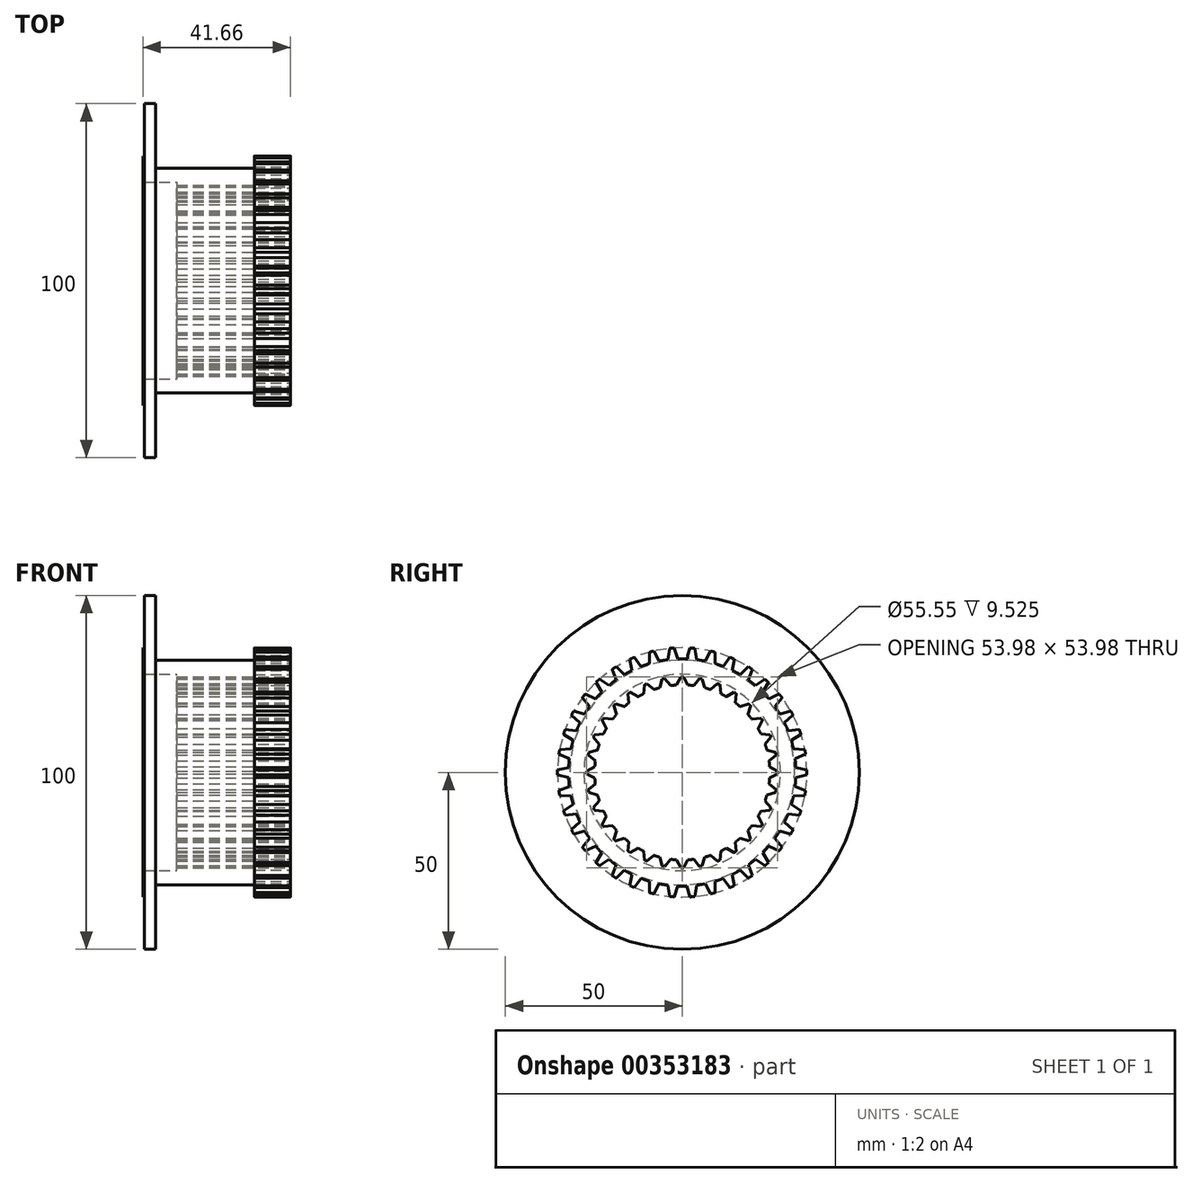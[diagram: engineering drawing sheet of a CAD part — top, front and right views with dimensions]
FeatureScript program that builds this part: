
annotation { "Feature Type Name" : "Feature", "Feature Type Description" : "" }
export const myFeature = defineFeature(function(context is Context, id is Id, definition is map)
    precondition{}
    {
        {
            var Q0;
            Q0=qCreatedBy(makeId("Front.planeOp"),FACE);
            var sketch = newSketch(context, id + "F0", { "sketchPlane" : qUnion([Q0])});
            skLineSegment(sketch, "E0", {"start": v(0, 0) * mm, "end": v(0, 35.24) * mm});
            skLineSegment(sketch, "E1", {"start": v(0, 35.24) * mm, "end": v(0.38, 35.24) * mm});
            skLineSegment(sketch, "E2", {"start": v(0.38, 35.24) * mm, "end": v(0.38, 50) * mm});
            skLineSegment(sketch, "E3", {"start": v(0.38, 50) * mm, "end": v(3.56, 50) * mm});
            skLineSegment(sketch, "E4", {"start": v(3.56, 50) * mm, "end": v(3.56, 31.75) * mm});
            skLineSegment(sketch, "E5", {"start": v(3.56, 31.75) * mm, "end": v(31.5, 31.75) * mm});
            skLineSegment(sketch, "E6", {"start": v(31.5, 31.75) * mm, "end": v(31.5, 35.24) * mm});
            skLineSegment(sketch, "E7", {"start": v(31.5, 35.24) * mm, "end": v(41.66, 35.24) * mm});
            skLineSegment(sketch, "E8", {"start": v(41.66, 35.24) * mm, "end": v(41.66, 0) * mm});
            skLineSegment(sketch, "E9", {"start": v(41.66, 0) * mm, "end": v(0, 0) * mm});
            skLineSegment(sketch, "E10", {"start": v(0, 27.77) * mm, "end": v(9.52, 27.77) * mm});
            skLineSegment(sketch, "E11", {"start": v(9.52, 27.77) * mm, "end": v(9.52, 24.77) * mm});
            skLineSegment(sketch, "E12", {"start": v(9.52, 24.77) * mm, "end": v(41.66, 24.77) * mm});
            skSolve(sketch);
        }
        {
            var Q0;
            {var subQ4=sQuery(id+"F0.wireOp",EDGE,"E1");Q0=makeQuery(id+"F0.imprint","IMPRINT",FACE,{"disambiguationData":[TD([[makeQuery(id+"F0.imprint","IMPRINT",EDGE,{"derivedFrom":subQ4}),-1.0]])]});}
            var Q1;
            Q1=sQuery(id+"F0.wireOp",EDGE,"E9");
            revolve(context, id + "F1", {"entities" : qUnion([Q0]), "axis" : qUnion([Q1]), "revolveType" : RevolveType.FULL});
        }
        {
            var Q0;
            Q0=makeQuery(id+"F1.opRevolve","SWEPT_FACE",FACE,{"disambiguationData":[OSD([sQuery(id+"F0.wireOp",EDGE,"E8")])]});
            var sketch = newSketch(context, id + "F2", { "sketchPlane" : qUnion([Q0])});
            skCircle(sketch, "E13", {"center": v(0, 0) * mm, "radius": 32.13 * mm});
            skLineSegment(sketch, "E14", {"start": v(-2.22, 35.17) * mm, "end": v(-1.27, 32.1) * mm});
            skLineSegment(sketch, "E15.MirrorCS", {"start": v(2.22, 35.17) * mm, "end": v(1.27, 32.1) * mm});
            skLineSegment(sketch, "E16.1.0", {"start": v(-7.98, 34.33) * mm, "end": v(-6.54, 31.46) * mm});
            skLineSegment(sketch, "E16.1.1", {"start": v(-3.6, 35.06) * mm, "end": v(-4.03, 31.88) * mm});
            skLineSegment(sketch, "E16.2.0", {"start": v(-13.52, 32.54) * mm, "end": v(-11.63, 29.95) * mm});
            skLineSegment(sketch, "E16.2.1", {"start": v(-9.32, 33.99) * mm, "end": v(-9.22, 30.78) * mm});
            skLineSegment(sketch, "E16.3.0", {"start": v(-18.7, 29.88) * mm, "end": v(-16.4, 27.63) * mm});
            skLineSegment(sketch, "E16.3.1", {"start": v(-14.79, 32) * mm, "end": v(-14.16, 28.84) * mm});
            skLineSegment(sketch, "E16.4.0", {"start": v(-23.36, 26.4) * mm, "end": v(-20.72, 24.56) * mm});
            skLineSegment(sketch, "E16.4.1", {"start": v(-19.85, 29.12) * mm, "end": v(-18.72, 26.12) * mm});
            skLineSegment(sketch, "E16.5.0", {"start": v(-27.38, 22.19) * mm, "end": v(-24.48, 20.81) * mm});
            skLineSegment(sketch, "E16.5.1", {"start": v(-24.37, 25.46) * mm, "end": v(-22.76, 22.68) * mm});
            skLineSegment(sketch, "E16.6.0", {"start": v(-30.66, 17.38) * mm, "end": v(-27.57, 16.5) * mm});
            skLineSegment(sketch, "E16.6.1", {"start": v(-28.23, 21.1) * mm, "end": v(-26.18, 18.62) * mm});
            skLineSegment(sketch, "E16.7.0", {"start": v(-33.1, 12.1) * mm, "end": v(-29.91, 11.73) * mm});
            skLineSegment(sketch, "E16.7.1", {"start": v(-31.32, 16.16) * mm, "end": v(-28.9, 14.06) * mm});
            skLineSegment(sketch, "E16.8.0", {"start": v(-34.64, 6.48) * mm, "end": v(-31.44, 6.65) * mm});
            skLineSegment(sketch, "E16.8.1", {"start": v(-33.55, 10.79) * mm, "end": v(-30.81, 9.11) * mm});
            skLineSegment(sketch, "E16.9.0", {"start": v(-35.24, 0.69) * mm, "end": v(-32.1, 1.39) * mm});
            skLineSegment(sketch, "E16.9.1", {"start": v(-34.87, 5.12) * mm, "end": v(-31.9, 3.92) * mm});
            skLineSegment(sketch, "E16.10.0", {"start": v(-34.87, -5.12) * mm, "end": v(-31.9, -3.92) * mm});
            skLineSegment(sketch, "E16.10.1", {"start": v(-35.24, -0.69) * mm, "end": v(-32.1, -1.39) * mm});
            skLineSegment(sketch, "E16.11.0", {"start": v(-33.55, -10.79) * mm, "end": v(-30.81, -9.11) * mm});
            skLineSegment(sketch, "E16.11.1", {"start": v(-34.64, -6.48) * mm, "end": v(-31.44, -6.65) * mm});
            skLineSegment(sketch, "E16.12.0", {"start": v(-31.32, -16.16) * mm, "end": v(-28.9, -14.06) * mm});
            skLineSegment(sketch, "E16.12.1", {"start": v(-33.1, -12.1) * mm, "end": v(-29.91, -11.73) * mm});
            skLineSegment(sketch, "E16.13.0", {"start": v(-28.23, -21.1) * mm, "end": v(-26.18, -18.62) * mm});
            skLineSegment(sketch, "E16.13.1", {"start": v(-30.66, -17.38) * mm, "end": v(-27.57, -16.5) * mm});
            skLineSegment(sketch, "E16.14.0", {"start": v(-24.37, -25.46) * mm, "end": v(-22.76, -22.68) * mm});
            skLineSegment(sketch, "E16.14.1", {"start": v(-27.38, -22.19) * mm, "end": v(-24.48, -20.81) * mm});
            skLineSegment(sketch, "E16.15.0", {"start": v(-19.85, -29.12) * mm, "end": v(-18.72, -26.12) * mm});
            skLineSegment(sketch, "E16.15.1", {"start": v(-23.36, -26.4) * mm, "end": v(-20.72, -24.56) * mm});
            skLineSegment(sketch, "E16.16.0", {"start": v(-14.79, -32) * mm, "end": v(-14.16, -28.84) * mm});
            skLineSegment(sketch, "E16.16.1", {"start": v(-18.7, -29.88) * mm, "end": v(-16.4, -27.63) * mm});
            skLineSegment(sketch, "E16.17.0", {"start": v(-9.32, -33.99) * mm, "end": v(-9.22, -30.78) * mm});
            skLineSegment(sketch, "E16.17.1", {"start": v(-13.52, -32.54) * mm, "end": v(-11.63, -29.95) * mm});
            skLineSegment(sketch, "E16.18.0", {"start": v(-3.6, -35.06) * mm, "end": v(-4.03, -31.88) * mm});
            skLineSegment(sketch, "E16.18.1", {"start": v(-7.98, -34.33) * mm, "end": v(-6.54, -31.46) * mm});
            skLineSegment(sketch, "E16.19.0", {"start": v(2.22, -35.17) * mm, "end": v(1.27, -32.1) * mm});
            skLineSegment(sketch, "E16.19.1", {"start": v(-2.22, -35.17) * mm, "end": v(-1.27, -32.1) * mm});
            skLineSegment(sketch, "E16.20.0", {"start": v(7.98, -34.33) * mm, "end": v(6.54, -31.46) * mm});
            skLineSegment(sketch, "E16.20.1", {"start": v(3.6, -35.06) * mm, "end": v(4.03, -31.88) * mm});
            skLineSegment(sketch, "E16.21.0", {"start": v(13.52, -32.54) * mm, "end": v(11.63, -29.95) * mm});
            skLineSegment(sketch, "E16.21.1", {"start": v(9.32, -33.99) * mm, "end": v(9.22, -30.78) * mm});
            skLineSegment(sketch, "E16.22.0", {"start": v(18.7, -29.88) * mm, "end": v(16.4, -27.63) * mm});
            skLineSegment(sketch, "E16.22.1", {"start": v(14.79, -32) * mm, "end": v(14.16, -28.84) * mm});
            skLineSegment(sketch, "E16.23.0", {"start": v(23.36, -26.4) * mm, "end": v(20.72, -24.56) * mm});
            skLineSegment(sketch, "E16.23.1", {"start": v(19.85, -29.12) * mm, "end": v(18.72, -26.12) * mm});
            skLineSegment(sketch, "E16.24.0", {"start": v(27.38, -22.19) * mm, "end": v(24.48, -20.81) * mm});
            skLineSegment(sketch, "E16.24.1", {"start": v(24.37, -25.46) * mm, "end": v(22.76, -22.68) * mm});
            skLineSegment(sketch, "E16.25.0", {"start": v(30.66, -17.38) * mm, "end": v(27.57, -16.5) * mm});
            skLineSegment(sketch, "E16.25.1", {"start": v(28.23, -21.1) * mm, "end": v(26.18, -18.62) * mm});
            skLineSegment(sketch, "E16.26.0", {"start": v(33.1, -12.1) * mm, "end": v(29.91, -11.73) * mm});
            skLineSegment(sketch, "E16.26.1", {"start": v(31.32, -16.16) * mm, "end": v(28.9, -14.06) * mm});
            skLineSegment(sketch, "E16.27.0", {"start": v(34.64, -6.48) * mm, "end": v(31.44, -6.65) * mm});
            skLineSegment(sketch, "E16.27.1", {"start": v(33.55, -10.79) * mm, "end": v(30.81, -9.11) * mm});
            skLineSegment(sketch, "E16.28.0", {"start": v(35.24, -0.69) * mm, "end": v(32.1, -1.39) * mm});
            skLineSegment(sketch, "E16.28.1", {"start": v(34.87, -5.12) * mm, "end": v(31.9, -3.92) * mm});
            skLineSegment(sketch, "E16.29.0", {"start": v(34.87, 5.12) * mm, "end": v(31.9, 3.92) * mm});
            skLineSegment(sketch, "E16.29.1", {"start": v(35.24, 0.69) * mm, "end": v(32.1, 1.39) * mm});
            skLineSegment(sketch, "E16.30.0", {"start": v(33.55, 10.79) * mm, "end": v(30.81, 9.11) * mm});
            skLineSegment(sketch, "E16.30.1", {"start": v(34.64, 6.48) * mm, "end": v(31.44, 6.65) * mm});
            skLineSegment(sketch, "E16.31.0", {"start": v(31.32, 16.16) * mm, "end": v(28.9, 14.06) * mm});
            skLineSegment(sketch, "E16.31.1", {"start": v(33.1, 12.1) * mm, "end": v(29.91, 11.73) * mm});
            skLineSegment(sketch, "E16.32.0", {"start": v(28.23, 21.1) * mm, "end": v(26.18, 18.62) * mm});
            skLineSegment(sketch, "E16.32.1", {"start": v(30.66, 17.38) * mm, "end": v(27.57, 16.5) * mm});
            skLineSegment(sketch, "E16.33.0", {"start": v(24.37, 25.46) * mm, "end": v(22.76, 22.68) * mm});
            skLineSegment(sketch, "E16.33.1", {"start": v(27.38, 22.19) * mm, "end": v(24.48, 20.81) * mm});
            skLineSegment(sketch, "E16.34.0", {"start": v(19.85, 29.12) * mm, "end": v(18.72, 26.12) * mm});
            skLineSegment(sketch, "E16.34.1", {"start": v(23.36, 26.4) * mm, "end": v(20.72, 24.56) * mm});
            skLineSegment(sketch, "E16.35.0", {"start": v(14.79, 32) * mm, "end": v(14.16, 28.84) * mm});
            skLineSegment(sketch, "E16.35.1", {"start": v(18.7, 29.88) * mm, "end": v(16.4, 27.63) * mm});
            skLineSegment(sketch, "E16.36.0", {"start": v(9.32, 33.99) * mm, "end": v(9.22, 30.78) * mm});
            skLineSegment(sketch, "E16.36.1", {"start": v(13.52, 32.54) * mm, "end": v(11.63, 29.95) * mm});
            skLineSegment(sketch, "E16.37.0", {"start": v(3.6, 35.06) * mm, "end": v(4.03, 31.88) * mm});
            skLineSegment(sketch, "E16.37.1", {"start": v(7.98, 34.33) * mm, "end": v(6.54, 31.46) * mm});
            skLineSegment(sketch, "E17", {"start": v(0, 0) * mm, "end": v(0, 59.65) * mm});
            skCircle(sketch, "E18", {"center": v(0, 0) * mm, "radius": 26.99 * mm});
            skLineSegment(sketch, "E19.0", {"start": v(0.38, 0) * mm, "end": v(0.38, 59.65) * mm});
            skLineSegment(sketch, "E20.0", {"start": v(1.57, 0) * mm, "end": v(1.57, 59.65) * mm});
            skLineSegment(sketch, "E21", {"start": v(0.38, 26.98) * mm, "end": v(1.57, 24.71) * mm});
            skLineSegment(sketch, "E22.MirrorCS", {"start": v(-0.38, 26.98) * mm, "end": v(-1.57, 24.71) * mm});
            skLineSegment(sketch, "E23.1.0", {"start": v(-5.64, 26.4) * mm, "end": v(-6.37, 23.93) * mm});
            skLineSegment(sketch, "E23.1.1", {"start": v(-4.9, 26.54) * mm, "end": v(-3.28, 24.55) * mm});
            skLineSegment(sketch, "E23.2.0", {"start": v(-10.68, 24.78) * mm, "end": v(-10.91, 22.23) * mm});
            skLineSegment(sketch, "E23.2.1", {"start": v(-9.97, 25.08) * mm, "end": v(-8, 23.44) * mm});
            skLineSegment(sketch, "E23.3.0", {"start": v(-15.3, 22.23) * mm, "end": v(-15.04, 19.67) * mm});
            skLineSegment(sketch, "E23.3.1", {"start": v(-14.68, 22.65) * mm, "end": v(-12.42, 21.42) * mm});
            skLineSegment(sketch, "E23.4.0", {"start": v(-19.35, 18.81) * mm, "end": v(-18.59, 16.36) * mm});
            skLineSegment(sketch, "E23.4.1", {"start": v(-18.81, 19.35) * mm, "end": v(-16.36, 18.59) * mm});
            skLineSegment(sketch, "E23.5.0", {"start": v(-22.65, 14.68) * mm, "end": v(-21.42, 12.42) * mm});
            skLineSegment(sketch, "E23.5.1", {"start": v(-22.23, 15.3) * mm, "end": v(-19.67, 15.04) * mm});
            skLineSegment(sketch, "E23.6.0", {"start": v(-25.08, 9.97) * mm, "end": v(-23.44, 8) * mm});
            skLineSegment(sketch, "E23.6.1", {"start": v(-24.78, 10.68) * mm, "end": v(-22.23, 10.91) * mm});
            skLineSegment(sketch, "E23.7.0", {"start": v(-26.54, 4.9) * mm, "end": v(-24.55, 3.28) * mm});
            skLineSegment(sketch, "E23.7.1", {"start": v(-26.4, 5.64) * mm, "end": v(-23.93, 6.37) * mm});
            skLineSegment(sketch, "E23.8.0", {"start": v(-26.98, -0.38) * mm, "end": v(-24.71, -1.57) * mm});
            skLineSegment(sketch, "E23.8.1", {"start": v(-26.98, 0.38) * mm, "end": v(-24.71, 1.57) * mm});
            skLineSegment(sketch, "E23.9.0", {"start": v(-26.4, -5.64) * mm, "end": v(-23.93, -6.37) * mm});
            skLineSegment(sketch, "E23.9.1", {"start": v(-26.54, -4.9) * mm, "end": v(-24.55, -3.28) * mm});
            skLineSegment(sketch, "E23.10.0", {"start": v(-24.78, -10.68) * mm, "end": v(-22.23, -10.91) * mm});
            skLineSegment(sketch, "E23.10.1", {"start": v(-25.08, -9.97) * mm, "end": v(-23.44, -8) * mm});
            skLineSegment(sketch, "E23.11.0", {"start": v(-22.23, -15.3) * mm, "end": v(-19.67, -15.04) * mm});
            skLineSegment(sketch, "E23.11.1", {"start": v(-22.65, -14.68) * mm, "end": v(-21.42, -12.42) * mm});
            skLineSegment(sketch, "E23.12.0", {"start": v(-18.81, -19.35) * mm, "end": v(-16.36, -18.59) * mm});
            skLineSegment(sketch, "E23.12.1", {"start": v(-19.35, -18.81) * mm, "end": v(-18.59, -16.36) * mm});
            skLineSegment(sketch, "E23.13.0", {"start": v(-14.68, -22.65) * mm, "end": v(-12.42, -21.42) * mm});
            skLineSegment(sketch, "E23.13.1", {"start": v(-15.3, -22.23) * mm, "end": v(-15.04, -19.67) * mm});
            skLineSegment(sketch, "E23.14.0", {"start": v(-9.97, -25.08) * mm, "end": v(-8, -23.44) * mm});
            skLineSegment(sketch, "E23.14.1", {"start": v(-10.68, -24.78) * mm, "end": v(-10.91, -22.23) * mm});
            skLineSegment(sketch, "E23.15.0", {"start": v(-4.9, -26.54) * mm, "end": v(-3.28, -24.55) * mm});
            skLineSegment(sketch, "E23.15.1", {"start": v(-5.64, -26.4) * mm, "end": v(-6.37, -23.93) * mm});
            skLineSegment(sketch, "E23.16.0", {"start": v(0.38, -26.98) * mm, "end": v(1.57, -24.71) * mm});
            skLineSegment(sketch, "E23.16.1", {"start": v(-0.38, -26.98) * mm, "end": v(-1.57, -24.71) * mm});
            skLineSegment(sketch, "E23.17.0", {"start": v(5.64, -26.4) * mm, "end": v(6.37, -23.93) * mm});
            skLineSegment(sketch, "E23.17.1", {"start": v(4.9, -26.54) * mm, "end": v(3.28, -24.55) * mm});
            skLineSegment(sketch, "E23.18.0", {"start": v(10.68, -24.78) * mm, "end": v(10.91, -22.23) * mm});
            skLineSegment(sketch, "E23.18.1", {"start": v(9.97, -25.08) * mm, "end": v(8, -23.44) * mm});
            skLineSegment(sketch, "E23.19.0", {"start": v(15.3, -22.23) * mm, "end": v(15.04, -19.67) * mm});
            skLineSegment(sketch, "E23.19.1", {"start": v(14.68, -22.65) * mm, "end": v(12.42, -21.42) * mm});
            skLineSegment(sketch, "E23.20.0", {"start": v(19.35, -18.81) * mm, "end": v(18.59, -16.36) * mm});
            skLineSegment(sketch, "E23.20.1", {"start": v(18.81, -19.35) * mm, "end": v(16.36, -18.59) * mm});
            skLineSegment(sketch, "E23.21.0", {"start": v(22.65, -14.68) * mm, "end": v(21.42, -12.42) * mm});
            skLineSegment(sketch, "E23.21.1", {"start": v(22.23, -15.3) * mm, "end": v(19.67, -15.04) * mm});
            skLineSegment(sketch, "E23.22.0", {"start": v(25.08, -9.97) * mm, "end": v(23.44, -8) * mm});
            skLineSegment(sketch, "E23.22.1", {"start": v(24.78, -10.68) * mm, "end": v(22.23, -10.91) * mm});
            skLineSegment(sketch, "E23.23.0", {"start": v(26.54, -4.9) * mm, "end": v(24.55, -3.28) * mm});
            skLineSegment(sketch, "E23.23.1", {"start": v(26.4, -5.64) * mm, "end": v(23.93, -6.37) * mm});
            skLineSegment(sketch, "E23.24.0", {"start": v(26.98, 0.38) * mm, "end": v(24.71, 1.57) * mm});
            skLineSegment(sketch, "E23.24.1", {"start": v(26.98, -0.38) * mm, "end": v(24.71, -1.57) * mm});
            skLineSegment(sketch, "E23.25.0", {"start": v(26.4, 5.64) * mm, "end": v(23.93, 6.37) * mm});
            skLineSegment(sketch, "E23.25.1", {"start": v(26.54, 4.9) * mm, "end": v(24.55, 3.28) * mm});
            skLineSegment(sketch, "E23.26.0", {"start": v(24.78, 10.68) * mm, "end": v(22.23, 10.91) * mm});
            skLineSegment(sketch, "E23.26.1", {"start": v(25.08, 9.97) * mm, "end": v(23.44, 8) * mm});
            skLineSegment(sketch, "E23.27.0", {"start": v(22.23, 15.3) * mm, "end": v(19.67, 15.04) * mm});
            skLineSegment(sketch, "E23.27.1", {"start": v(22.65, 14.68) * mm, "end": v(21.42, 12.42) * mm});
            skLineSegment(sketch, "E23.28.0", {"start": v(18.81, 19.35) * mm, "end": v(16.36, 18.59) * mm});
            skLineSegment(sketch, "E23.28.1", {"start": v(19.35, 18.81) * mm, "end": v(18.59, 16.36) * mm});
            skLineSegment(sketch, "E23.29.0", {"start": v(14.68, 22.65) * mm, "end": v(12.42, 21.42) * mm});
            skLineSegment(sketch, "E23.29.1", {"start": v(15.3, 22.23) * mm, "end": v(15.04, 19.67) * mm});
            skLineSegment(sketch, "E23.30.0", {"start": v(9.97, 25.08) * mm, "end": v(8, 23.44) * mm});
            skLineSegment(sketch, "E23.30.1", {"start": v(10.68, 24.78) * mm, "end": v(10.91, 22.23) * mm});
            skLineSegment(sketch, "E23.31.0", {"start": v(4.9, 26.54) * mm, "end": v(3.28, 24.55) * mm});
            skLineSegment(sketch, "E23.31.1", {"start": v(5.64, 26.4) * mm, "end": v(6.37, 23.93) * mm});
            skSolve(sketch);
        }
        {
            var Q0;
            {var subQ0=sQuery(id+"F2.wireOp",EDGE,"E16.2.0");Q0=makeQuery(id+"F2.imprint","IMPRINT",FACE,{"disambiguationData":[TD([[makeQuery(id+"F2.imprint","IMPRINT",EDGE,{"derivedFrom":subQ0}),1.0]])]});}
            var Q1;
            {var subQ0=sQuery(id+"F2.wireOp",EDGE,"E16.1.0");Q1=makeQuery(id+"F2.imprint","IMPRINT",FACE,{"disambiguationData":[TD([[makeQuery(id+"F2.imprint","IMPRINT",EDGE,{"derivedFrom":subQ0}),1.0]])]});}
            var Q2;
            {var subQ0=sQuery(id+"F2.wireOp",EDGE,"E15.MirrorCS");Q2=makeQuery(id+"F2.imprint","IMPRINT",FACE,{"disambiguationData":[TD([[makeQuery(id+"F2.imprint","IMPRINT",EDGE,{"derivedFrom":subQ0}),-1.0]])]});}
            var Q3;
            {var subQ1=sQuery(id+"F2.wireOp",EDGE,"E13");var subQ3=sQuery(id+"F2.wireOp",EDGE,"tALtZrFu-aeeX-mBGS-Ck9h-40K6PGTT2Hge");var subQ4=makeQuery(id+"F2.imprint","INTERSECT",VERTEX,{"derivedFrom":[subQ1,subQ3]});Q3=makeQuery(id+"F2.imprint","IMPRINT",FACE,{"disambiguationData":[TD([[makeQuery(id+"F2.imprint","IMPRINT",EDGE,{"disambiguationData":[TD([[subQ4,-1.0]])],"derivedFrom":subQ1}),-1.0]])]});}
            var Q4;
            {var subQ0=sQuery(id+"F2.wireOp",EDGE,"E14");Q4=makeQuery(id+"F2.imprint","IMPRINT",FACE,{"disambiguationData":[TD([[makeQuery(id+"F2.imprint","IMPRINT",EDGE,{"derivedFrom":subQ0}),1.0]])]});}
            var Q5;
            {var subQ0=sQuery(id+"F2.wireOp",EDGE,"E16.37.0");Q5=makeQuery(id+"F2.imprint","IMPRINT",FACE,{"disambiguationData":[TD([[makeQuery(id+"F2.imprint","IMPRINT",EDGE,{"derivedFrom":subQ0}),1.0]])]});}
            var Q6;
            {var subQ0=sQuery(id+"F2.wireOp",EDGE,"E16.36.0");Q6=makeQuery(id+"F2.imprint","IMPRINT",FACE,{"disambiguationData":[TD([[makeQuery(id+"F2.imprint","IMPRINT",EDGE,{"derivedFrom":subQ0}),1.0]])]});}
            var Q7;
            {var subQ0=sQuery(id+"F2.wireOp",EDGE,"E16.35.0");Q7=makeQuery(id+"F2.imprint","IMPRINT",FACE,{"disambiguationData":[TD([[makeQuery(id+"F2.imprint","IMPRINT",EDGE,{"derivedFrom":subQ0}),1.0]])]});}
            var Q8;
            {var subQ0=sQuery(id+"F2.wireOp",EDGE,"E16.34.0");Q8=makeQuery(id+"F2.imprint","IMPRINT",FACE,{"disambiguationData":[TD([[makeQuery(id+"F2.imprint","IMPRINT",EDGE,{"derivedFrom":subQ0}),1.0]])]});}
            var Q9;
            {var subQ0=sQuery(id+"F2.wireOp",EDGE,"E16.33.0");Q9=makeQuery(id+"F2.imprint","IMPRINT",FACE,{"disambiguationData":[TD([[makeQuery(id+"F2.imprint","IMPRINT",EDGE,{"derivedFrom":subQ0}),1.0]])]});}
            var Q10;
            {var subQ0=sQuery(id+"F2.wireOp",EDGE,"E16.32.0");Q10=makeQuery(id+"F2.imprint","IMPRINT",FACE,{"disambiguationData":[TD([[makeQuery(id+"F2.imprint","IMPRINT",EDGE,{"derivedFrom":subQ0}),1.0]])]});}
            var Q11;
            {var subQ0=sQuery(id+"F2.wireOp",EDGE,"E16.31.0");Q11=makeQuery(id+"F2.imprint","IMPRINT",FACE,{"disambiguationData":[TD([[makeQuery(id+"F2.imprint","IMPRINT",EDGE,{"derivedFrom":subQ0}),1.0]])]});}
            var Q12;
            {var subQ0=sQuery(id+"F2.wireOp",EDGE,"E16.30.0");Q12=makeQuery(id+"F2.imprint","IMPRINT",FACE,{"disambiguationData":[TD([[makeQuery(id+"F2.imprint","IMPRINT",EDGE,{"derivedFrom":subQ0}),1.0]])]});}
            var Q13;
            {var subQ0=sQuery(id+"F2.wireOp",EDGE,"E16.29.0");Q13=makeQuery(id+"F2.imprint","IMPRINT",FACE,{"disambiguationData":[TD([[makeQuery(id+"F2.imprint","IMPRINT",EDGE,{"derivedFrom":subQ0}),1.0]])]});}
            var Q14;
            {var subQ0=sQuery(id+"F2.wireOp",EDGE,"E16.28.0");Q14=makeQuery(id+"F2.imprint","IMPRINT",FACE,{"disambiguationData":[TD([[makeQuery(id+"F2.imprint","IMPRINT",EDGE,{"derivedFrom":subQ0}),1.0]])]});}
            var Q15;
            {var subQ0=sQuery(id+"F2.wireOp",EDGE,"E16.27.0");Q15=makeQuery(id+"F2.imprint","IMPRINT",FACE,{"disambiguationData":[TD([[makeQuery(id+"F2.imprint","IMPRINT",EDGE,{"derivedFrom":subQ0}),1.0]])]});}
            var Q16;
            {var subQ0=sQuery(id+"F2.wireOp",EDGE,"E16.26.0");Q16=makeQuery(id+"F2.imprint","IMPRINT",FACE,{"disambiguationData":[TD([[makeQuery(id+"F2.imprint","IMPRINT",EDGE,{"derivedFrom":subQ0}),1.0]])]});}
            var Q17;
            {var subQ0=sQuery(id+"F2.wireOp",EDGE,"E16.25.0");Q17=makeQuery(id+"F2.imprint","IMPRINT",FACE,{"disambiguationData":[TD([[makeQuery(id+"F2.imprint","IMPRINT",EDGE,{"derivedFrom":subQ0}),1.0]])]});}
            var Q18;
            {var subQ0=sQuery(id+"F2.wireOp",EDGE,"E16.24.0");Q18=makeQuery(id+"F2.imprint","IMPRINT",FACE,{"disambiguationData":[TD([[makeQuery(id+"F2.imprint","IMPRINT",EDGE,{"derivedFrom":subQ0}),1.0]])]});}
            var Q19;
            {var subQ0=sQuery(id+"F2.wireOp",EDGE,"E16.23.0");Q19=makeQuery(id+"F2.imprint","IMPRINT",FACE,{"disambiguationData":[TD([[makeQuery(id+"F2.imprint","IMPRINT",EDGE,{"derivedFrom":subQ0}),1.0]])]});}
            var Q20;
            {var subQ0=sQuery(id+"F2.wireOp",EDGE,"E16.22.0");Q20=makeQuery(id+"F2.imprint","IMPRINT",FACE,{"disambiguationData":[TD([[makeQuery(id+"F2.imprint","IMPRINT",EDGE,{"derivedFrom":subQ0}),1.0]])]});}
            var Q21;
            {var subQ0=sQuery(id+"F2.wireOp",EDGE,"E16.21.0");Q21=makeQuery(id+"F2.imprint","IMPRINT",FACE,{"disambiguationData":[TD([[makeQuery(id+"F2.imprint","IMPRINT",EDGE,{"derivedFrom":subQ0}),1.0]])]});}
            var Q22;
            {var subQ0=sQuery(id+"F2.wireOp",EDGE,"E16.20.0");Q22=makeQuery(id+"F2.imprint","IMPRINT",FACE,{"disambiguationData":[TD([[makeQuery(id+"F2.imprint","IMPRINT",EDGE,{"derivedFrom":subQ0}),1.0]])]});}
            var Q23;
            {var subQ0=sQuery(id+"F2.wireOp",EDGE,"E16.19.0");Q23=makeQuery(id+"F2.imprint","IMPRINT",FACE,{"disambiguationData":[TD([[makeQuery(id+"F2.imprint","IMPRINT",EDGE,{"derivedFrom":subQ0}),1.0]])]});}
            var Q24;
            {var subQ0=sQuery(id+"F2.wireOp",EDGE,"E16.18.0");Q24=makeQuery(id+"F2.imprint","IMPRINT",FACE,{"disambiguationData":[TD([[makeQuery(id+"F2.imprint","IMPRINT",EDGE,{"derivedFrom":subQ0}),1.0]])]});}
            var Q25;
            {var subQ0=sQuery(id+"F2.wireOp",EDGE,"E16.17.0");Q25=makeQuery(id+"F2.imprint","IMPRINT",FACE,{"disambiguationData":[TD([[makeQuery(id+"F2.imprint","IMPRINT",EDGE,{"derivedFrom":subQ0}),1.0]])]});}
            var Q26;
            {var subQ0=sQuery(id+"F2.wireOp",EDGE,"E16.16.0");Q26=makeQuery(id+"F2.imprint","IMPRINT",FACE,{"disambiguationData":[TD([[makeQuery(id+"F2.imprint","IMPRINT",EDGE,{"derivedFrom":subQ0}),1.0]])]});}
            var Q27;
            {var subQ0=sQuery(id+"F2.wireOp",EDGE,"E16.15.0");Q27=makeQuery(id+"F2.imprint","IMPRINT",FACE,{"disambiguationData":[TD([[makeQuery(id+"F2.imprint","IMPRINT",EDGE,{"derivedFrom":subQ0}),1.0]])]});}
            var Q28;
            {var subQ0=sQuery(id+"F2.wireOp",EDGE,"E16.14.0");Q28=makeQuery(id+"F2.imprint","IMPRINT",FACE,{"disambiguationData":[TD([[makeQuery(id+"F2.imprint","IMPRINT",EDGE,{"derivedFrom":subQ0}),1.0]])]});}
            var Q29;
            {var subQ0=sQuery(id+"F2.wireOp",EDGE,"E16.13.0");Q29=makeQuery(id+"F2.imprint","IMPRINT",FACE,{"disambiguationData":[TD([[makeQuery(id+"F2.imprint","IMPRINT",EDGE,{"derivedFrom":subQ0}),1.0]])]});}
            var Q30;
            {var subQ0=sQuery(id+"F2.wireOp",EDGE,"E16.12.0");Q30=makeQuery(id+"F2.imprint","IMPRINT",FACE,{"disambiguationData":[TD([[makeQuery(id+"F2.imprint","IMPRINT",EDGE,{"derivedFrom":subQ0}),1.0]])]});}
            var Q31;
            {var subQ0=sQuery(id+"F2.wireOp",EDGE,"E16.11.0");Q31=makeQuery(id+"F2.imprint","IMPRINT",FACE,{"disambiguationData":[TD([[makeQuery(id+"F2.imprint","IMPRINT",EDGE,{"derivedFrom":subQ0}),1.0]])]});}
            var Q32;
            {var subQ0=sQuery(id+"F2.wireOp",EDGE,"E16.10.0");Q32=makeQuery(id+"F2.imprint","IMPRINT",FACE,{"disambiguationData":[TD([[makeQuery(id+"F2.imprint","IMPRINT",EDGE,{"derivedFrom":subQ0}),1.0]])]});}
            var Q33;
            {var subQ0=sQuery(id+"F2.wireOp",EDGE,"E16.9.0");Q33=makeQuery(id+"F2.imprint","IMPRINT",FACE,{"disambiguationData":[TD([[makeQuery(id+"F2.imprint","IMPRINT",EDGE,{"derivedFrom":subQ0}),1.0]])]});}
            var Q34;
            {var subQ0=sQuery(id+"F2.wireOp",EDGE,"E16.8.0");Q34=makeQuery(id+"F2.imprint","IMPRINT",FACE,{"disambiguationData":[TD([[makeQuery(id+"F2.imprint","IMPRINT",EDGE,{"derivedFrom":subQ0}),1.0]])]});}
            var Q35;
            {var subQ0=sQuery(id+"F2.wireOp",EDGE,"E16.7.0");Q35=makeQuery(id+"F2.imprint","IMPRINT",FACE,{"disambiguationData":[TD([[makeQuery(id+"F2.imprint","IMPRINT",EDGE,{"derivedFrom":subQ0}),1.0]])]});}
            var Q36;
            {var subQ0=sQuery(id+"F2.wireOp",EDGE,"E16.6.0");Q36=makeQuery(id+"F2.imprint","IMPRINT",FACE,{"disambiguationData":[TD([[makeQuery(id+"F2.imprint","IMPRINT",EDGE,{"derivedFrom":subQ0}),1.0]])]});}
            var Q37;
            {var subQ0=sQuery(id+"F2.wireOp",EDGE,"E16.5.0");Q37=makeQuery(id+"F2.imprint","IMPRINT",FACE,{"disambiguationData":[TD([[makeQuery(id+"F2.imprint","IMPRINT",EDGE,{"derivedFrom":subQ0}),1.0]])]});}
            var Q38;
            {var subQ0=sQuery(id+"F2.wireOp",EDGE,"E16.4.0");Q38=makeQuery(id+"F2.imprint","IMPRINT",FACE,{"disambiguationData":[TD([[makeQuery(id+"F2.imprint","IMPRINT",EDGE,{"derivedFrom":subQ0}),1.0]])]});}
            var Q39;
            {var subQ0=sQuery(id+"F2.wireOp",EDGE,"E16.3.0");Q39=makeQuery(id+"F2.imprint","IMPRINT",FACE,{"disambiguationData":[TD([[makeQuery(id+"F2.imprint","IMPRINT",EDGE,{"derivedFrom":subQ0}),1.0]])]});}
            var Q40;
            {var subQ1=sQuery(id+"F2.wireOp",EDGE,"E13");var subQ5=sQuery(id+"F2.wireOp",EDGE,"E15.MirrorCS");var subQ6=makeQuery(id+"F2.imprint","INTERSECT",VERTEX,{"derivedFrom":[subQ1,subQ5]});Q40=makeQuery(id+"F2.imprint","IMPRINT",FACE,{"disambiguationData":[TD([[makeQuery(id+"F2.imprint","IMPRINT",EDGE,{"disambiguationData":[TD([[subQ6,-1.0]])],"derivedFrom":subQ1}),-1.0]])]});}
            var Q41;
            {var subQ0=sQuery(id+"F2.wireOp",EDGE,"E19.0");var subQ1=sQuery(id+"F2.wireOp",EDGE,"E13");var subQ2=makeQuery(id+"F2.imprint","INTERSECT",VERTEX,{"derivedFrom":[subQ1,subQ0]});Q41=makeQuery(id+"F2.imprint","IMPRINT",FACE,{"disambiguationData":[TD([[makeQuery(id+"F2.imprint","IMPRINT",EDGE,{"disambiguationData":[TD([[subQ2,-1.0]])],"derivedFrom":subQ1}),-1.0]])]});}
            var Q42;
            {var subQ5=sQuery(id+"F2.wireOp",EDGE,"E22.MirrorCS");Q42=makeQuery(id+"F2.imprint","IMPRINT",FACE,{"disambiguationData":[TD([[makeQuery(id+"F2.imprint","IMPRINT",EDGE,{"derivedFrom":subQ5}),1.0]])]});}
            var Q43;
            {var subQ0=sQuery(id+"F2.wireOp",EDGE,"E18");var subQ1=sQuery(id+"F2.wireOp",EDGE,"E17");var subQ2=makeQuery(id+"F2.imprint","INTERSECT",VERTEX,{"derivedFrom":[subQ1,subQ0]});Q43=makeQuery(id+"F2.imprint","IMPRINT",FACE,{"disambiguationData":[TD([[makeQuery(id+"F2.imprint","IMPRINT",EDGE,{"disambiguationData":[TD([[subQ2,1.0]])],"derivedFrom":subQ1}),-1.0]])]});}
            var Q44;
            {var subQ0=sQuery(id+"F2.wireOp",EDGE,"E21");Q44=makeQuery(id+"F2.imprint","IMPRINT",FACE,{"disambiguationData":[TD([[makeQuery(id+"F2.imprint","IMPRINT",EDGE,{"derivedFrom":subQ0}),-1.0]])]});}
            var Q45;
            {var subQ0=sQuery(id+"F2.wireOp",EDGE,"E23.31.0");Q45=makeQuery(id+"F2.imprint","IMPRINT",FACE,{"disambiguationData":[TD([[makeQuery(id+"F2.imprint","IMPRINT",EDGE,{"derivedFrom":subQ0}),1.0]])]});}
            var Q46;
            {var subQ0=sQuery(id+"F2.wireOp",EDGE,"E23.30.0");Q46=makeQuery(id+"F2.imprint","IMPRINT",FACE,{"disambiguationData":[TD([[makeQuery(id+"F2.imprint","IMPRINT",EDGE,{"derivedFrom":subQ0}),1.0]])]});}
            var Q47;
            {var subQ0=sQuery(id+"F2.wireOp",EDGE,"E23.29.0");Q47=makeQuery(id+"F2.imprint","IMPRINT",FACE,{"disambiguationData":[TD([[makeQuery(id+"F2.imprint","IMPRINT",EDGE,{"derivedFrom":subQ0}),1.0]])]});}
            var Q48;
            {var subQ0=sQuery(id+"F2.wireOp",EDGE,"E23.1.0");Q48=makeQuery(id+"F2.imprint","IMPRINT",FACE,{"disambiguationData":[TD([[makeQuery(id+"F2.imprint","IMPRINT",EDGE,{"derivedFrom":subQ0}),1.0]])]});}
            var Q49;
            {var subQ0=sQuery(id+"F2.wireOp",EDGE,"E23.2.0");Q49=makeQuery(id+"F2.imprint","IMPRINT",FACE,{"disambiguationData":[TD([[makeQuery(id+"F2.imprint","IMPRINT",EDGE,{"derivedFrom":subQ0}),1.0]])]});}
            var Q50;
            {var subQ0=sQuery(id+"F2.wireOp",EDGE,"E23.3.0");Q50=makeQuery(id+"F2.imprint","IMPRINT",FACE,{"disambiguationData":[TD([[makeQuery(id+"F2.imprint","IMPRINT",EDGE,{"derivedFrom":subQ0}),1.0]])]});}
            var Q51;
            {var subQ0=sQuery(id+"F2.wireOp",EDGE,"E23.28.0");Q51=makeQuery(id+"F2.imprint","IMPRINT",FACE,{"disambiguationData":[TD([[makeQuery(id+"F2.imprint","IMPRINT",EDGE,{"derivedFrom":subQ0}),1.0]])]});}
            var Q52;
            {var subQ0=sQuery(id+"F2.wireOp",EDGE,"E23.27.0");Q52=makeQuery(id+"F2.imprint","IMPRINT",FACE,{"disambiguationData":[TD([[makeQuery(id+"F2.imprint","IMPRINT",EDGE,{"derivedFrom":subQ0}),1.0]])]});}
            var Q53;
            {var subQ0=sQuery(id+"F2.wireOp",EDGE,"E23.26.0");Q53=makeQuery(id+"F2.imprint","IMPRINT",FACE,{"disambiguationData":[TD([[makeQuery(id+"F2.imprint","IMPRINT",EDGE,{"derivedFrom":subQ0}),1.0]])]});}
            var Q54;
            {var subQ0=sQuery(id+"F2.wireOp",EDGE,"E23.25.0");Q54=makeQuery(id+"F2.imprint","IMPRINT",FACE,{"disambiguationData":[TD([[makeQuery(id+"F2.imprint","IMPRINT",EDGE,{"derivedFrom":subQ0}),1.0]])]});}
            var Q55;
            {var subQ0=sQuery(id+"F2.wireOp",EDGE,"E23.24.0");Q55=makeQuery(id+"F2.imprint","IMPRINT",FACE,{"disambiguationData":[TD([[makeQuery(id+"F2.imprint","IMPRINT",EDGE,{"derivedFrom":subQ0}),1.0]])]});}
            var Q56;
            {var subQ0=sQuery(id+"F2.wireOp",EDGE,"E23.23.0");Q56=makeQuery(id+"F2.imprint","IMPRINT",FACE,{"disambiguationData":[TD([[makeQuery(id+"F2.imprint","IMPRINT",EDGE,{"derivedFrom":subQ0}),1.0]])]});}
            var Q57;
            {var subQ0=sQuery(id+"F2.wireOp",EDGE,"E23.22.0");Q57=makeQuery(id+"F2.imprint","IMPRINT",FACE,{"disambiguationData":[TD([[makeQuery(id+"F2.imprint","IMPRINT",EDGE,{"derivedFrom":subQ0}),1.0]])]});}
            var Q58;
            {var subQ0=sQuery(id+"F2.wireOp",EDGE,"E23.21.0");Q58=makeQuery(id+"F2.imprint","IMPRINT",FACE,{"disambiguationData":[TD([[makeQuery(id+"F2.imprint","IMPRINT",EDGE,{"derivedFrom":subQ0}),1.0]])]});}
            var Q59;
            {var subQ0=sQuery(id+"F2.wireOp",EDGE,"E23.20.0");Q59=makeQuery(id+"F2.imprint","IMPRINT",FACE,{"disambiguationData":[TD([[makeQuery(id+"F2.imprint","IMPRINT",EDGE,{"derivedFrom":subQ0}),1.0]])]});}
            var Q60;
            {var subQ0=sQuery(id+"F2.wireOp",EDGE,"E23.19.0");Q60=makeQuery(id+"F2.imprint","IMPRINT",FACE,{"disambiguationData":[TD([[makeQuery(id+"F2.imprint","IMPRINT",EDGE,{"derivedFrom":subQ0}),1.0]])]});}
            var Q61;
            {var subQ0=sQuery(id+"F2.wireOp",EDGE,"E23.18.0");Q61=makeQuery(id+"F2.imprint","IMPRINT",FACE,{"disambiguationData":[TD([[makeQuery(id+"F2.imprint","IMPRINT",EDGE,{"derivedFrom":subQ0}),1.0]])]});}
            var Q62;
            {var subQ0=sQuery(id+"F2.wireOp",EDGE,"E23.17.0");Q62=makeQuery(id+"F2.imprint","IMPRINT",FACE,{"disambiguationData":[TD([[makeQuery(id+"F2.imprint","IMPRINT",EDGE,{"derivedFrom":subQ0}),1.0]])]});}
            var Q63;
            {var subQ0=sQuery(id+"F2.wireOp",EDGE,"E23.16.0");Q63=makeQuery(id+"F2.imprint","IMPRINT",FACE,{"disambiguationData":[TD([[makeQuery(id+"F2.imprint","IMPRINT",EDGE,{"derivedFrom":subQ0}),1.0]])]});}
            var Q64;
            {var subQ0=sQuery(id+"F2.wireOp",EDGE,"E23.15.0");Q64=makeQuery(id+"F2.imprint","IMPRINT",FACE,{"disambiguationData":[TD([[makeQuery(id+"F2.imprint","IMPRINT",EDGE,{"derivedFrom":subQ0}),1.0]])]});}
            var Q65;
            {var subQ0=sQuery(id+"F2.wireOp",EDGE,"E23.14.0");Q65=makeQuery(id+"F2.imprint","IMPRINT",FACE,{"disambiguationData":[TD([[makeQuery(id+"F2.imprint","IMPRINT",EDGE,{"derivedFrom":subQ0}),1.0]])]});}
            var Q66;
            {var subQ0=sQuery(id+"F2.wireOp",EDGE,"E23.13.0");Q66=makeQuery(id+"F2.imprint","IMPRINT",FACE,{"disambiguationData":[TD([[makeQuery(id+"F2.imprint","IMPRINT",EDGE,{"derivedFrom":subQ0}),1.0]])]});}
            var Q67;
            {var subQ0=sQuery(id+"F2.wireOp",EDGE,"E23.12.0");Q67=makeQuery(id+"F2.imprint","IMPRINT",FACE,{"disambiguationData":[TD([[makeQuery(id+"F2.imprint","IMPRINT",EDGE,{"derivedFrom":subQ0}),1.0]])]});}
            var Q68;
            {var subQ0=sQuery(id+"F2.wireOp",EDGE,"E23.11.0");Q68=makeQuery(id+"F2.imprint","IMPRINT",FACE,{"disambiguationData":[TD([[makeQuery(id+"F2.imprint","IMPRINT",EDGE,{"derivedFrom":subQ0}),1.0]])]});}
            var Q69;
            {var subQ0=sQuery(id+"F2.wireOp",EDGE,"E23.10.0");Q69=makeQuery(id+"F2.imprint","IMPRINT",FACE,{"disambiguationData":[TD([[makeQuery(id+"F2.imprint","IMPRINT",EDGE,{"derivedFrom":subQ0}),1.0]])]});}
            var Q70;
            {var subQ0=sQuery(id+"F2.wireOp",EDGE,"E23.9.0");Q70=makeQuery(id+"F2.imprint","IMPRINT",FACE,{"disambiguationData":[TD([[makeQuery(id+"F2.imprint","IMPRINT",EDGE,{"derivedFrom":subQ0}),1.0]])]});}
            var Q71;
            {var subQ0=sQuery(id+"F2.wireOp",EDGE,"E23.8.0");Q71=makeQuery(id+"F2.imprint","IMPRINT",FACE,{"disambiguationData":[TD([[makeQuery(id+"F2.imprint","IMPRINT",EDGE,{"derivedFrom":subQ0}),1.0]])]});}
            var Q72;
            {var subQ0=sQuery(id+"F2.wireOp",EDGE,"E23.7.0");Q72=makeQuery(id+"F2.imprint","IMPRINT",FACE,{"disambiguationData":[TD([[makeQuery(id+"F2.imprint","IMPRINT",EDGE,{"derivedFrom":subQ0}),1.0]])]});}
            var Q73;
            {var subQ0=sQuery(id+"F2.wireOp",EDGE,"E23.6.0");Q73=makeQuery(id+"F2.imprint","IMPRINT",FACE,{"disambiguationData":[TD([[makeQuery(id+"F2.imprint","IMPRINT",EDGE,{"derivedFrom":subQ0}),1.0]])]});}
            var Q74;
            {var subQ0=sQuery(id+"F2.wireOp",EDGE,"E23.5.0");Q74=makeQuery(id+"F2.imprint","IMPRINT",FACE,{"disambiguationData":[TD([[makeQuery(id+"F2.imprint","IMPRINT",EDGE,{"derivedFrom":subQ0}),1.0]])]});}
            var Q75;
            {var subQ0=sQuery(id+"F2.wireOp",EDGE,"E23.4.0");Q75=makeQuery(id+"F2.imprint","IMPRINT",FACE,{"disambiguationData":[TD([[makeQuery(id+"F2.imprint","IMPRINT",EDGE,{"derivedFrom":subQ0}),1.0]])]});}
            extrude(context, id + "F3", {"entities" : qUnion([Q0, Q1, Q2, Q3, Q4, Q5, Q6, Q7, Q8, Q9, Q10, Q11, Q12, Q13, Q14, Q15, Q16, Q17, Q18, Q19, Q20, Q21, Q22, Q23, Q24, Q25, Q26, Q27, Q28, Q29, Q30, Q31, Q32, Q33, Q34, Q35, Q36, Q37, Q38, Q39, Q40, Q41, Q42, Q43, Q44, Q45, Q46, Q47, Q48, Q49, Q50, Q51, Q52, Q53, Q54, Q55, Q56, Q57, Q58, Q59, Q60, Q61, Q62, Q63, Q64, Q65, Q66, Q67, Q68, Q69, Q70, Q71, Q72, Q73, Q74, Q75]), "operationType" : NewBodyOperationType.REMOVE, "endBound" : BoundingType.UP_TO_NEXT, "oppositeDirection" : true, "depth" : 25.4 * mm});
        }
    });
